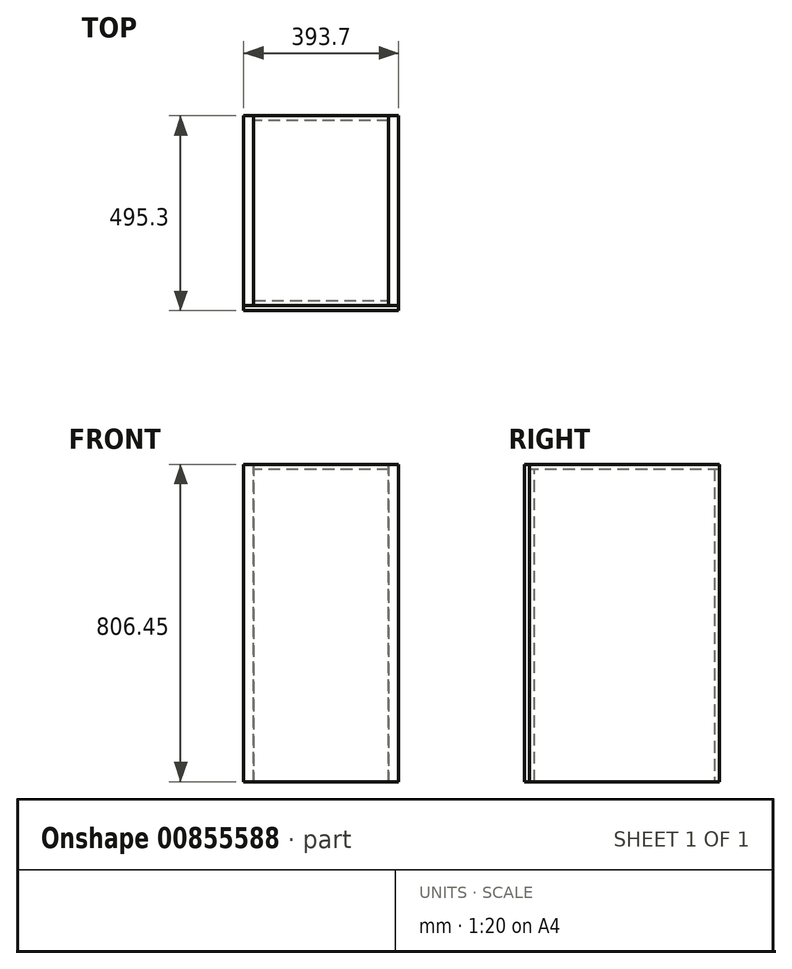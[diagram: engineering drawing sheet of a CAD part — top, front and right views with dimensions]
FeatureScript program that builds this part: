
annotation { "Feature Type Name" : "Feature", "Feature Type Description" : "" }
export const myFeature = defineFeature(function(context is Context, id is Id, definition is map)
    precondition{}
    {
        {
            var Q0;
            Q0=qCreatedBy(makeId("Front.planeOp"),FACE);
            var sketch = newSketch(context, id + "F0", { "sketchPlane" : qUnion([Q0])});
            skLineSegment(sketch, "E0.bottom", {"start": v(288.56, 543.22) * mm, "end": v(-105.14, 543.22) * mm});
            skLineSegment(sketch, "E0.top", {"start": v(288.56, -263.23) * mm, "end": v(-105.14, -263.23) * mm});
            skLineSegment(sketch, "E0.left", {"start": v(288.56, 543.22) * mm, "end": v(288.56, -263.23) * mm});
            skLineSegment(sketch, "E0.right", {"start": v(-105.14, 543.22) * mm, "end": v(-105.14, -263.23) * mm});
            skSolve(sketch);
        }
        {
            var Q0;
            Q0=makeQuery(id+"F0.imprint","IMPRINT",FACE,{"disambiguationData":[TD([[makeQuery(id+"F0.imprint","IMPRINT",EDGE,{"derivedFrom":sQuery(id+"F0.wireOp",EDGE,"E0.bottom")}),1.0]])]});
            var sketch = newSketch(context, id + "F1", { "sketchPlane" : qUnion([Q0])});
            skLineSegment(sketch, "E1.bottom", {"start": v(-105.14, 543.22) * mm, "end": v(-79.74, 543.22) * mm});
            skLineSegment(sketch, "E1.top", {"start": v(-105.14, -263.23) * mm, "end": v(-79.74, -263.23) * mm});
            skLineSegment(sketch, "E1.left", {"start": v(-105.14, 543.22) * mm, "end": v(-105.14, -263.23) * mm});
            skLineSegment(sketch, "E1.right", {"start": v(-79.74, 543.22) * mm, "end": v(-79.74, -263.23) * mm});
            skLineSegment(sketch, "E2.bottom", {"start": v(263.16, 543.22) * mm, "end": v(288.56, 543.22) * mm});
            skLineSegment(sketch, "E2.top", {"start": v(263.16, -263.23) * mm, "end": v(288.56, -263.23) * mm});
            skLineSegment(sketch, "E2.left", {"start": v(263.16, 543.22) * mm, "end": v(263.16, -263.23) * mm});
            skLineSegment(sketch, "E2.right", {"start": v(288.56, 543.22) * mm, "end": v(288.56, -263.23) * mm});
            skSolve(sketch);
        }
        {
            var Q0;
            Q0 = qSketchRegion(id + "F1", true);
            extrude(context, id + "F2", {"entities" : qUnion([Q0]), "depth" : 482.6 * mm, "offsetDistance" : 25.4 * mm});
        }
        {
            var Q0;
            Q0=makeQuery(id+"F2.opExtrude","CAP_FACE",FACE,{"disambiguationData":[OSD([sQuery(id+"F1.wireOp",EDGE,"E1.bottom"),sQuery(id+"F1.wireOp",EDGE,"E1.top"),sQuery(id+"F1.wireOp",EDGE,"E1.left"),sQuery(id+"F1.wireOp",EDGE,"E1.right")])],"isStart":false});
            var sketch = newSketch(context, id + "F3", { "sketchPlane" : qUnion([Q0])});
            skLineSegment(sketch, "E3.bottom", {"start": v(-79.74, 543.22) * mm, "end": v(263.16, 543.22) * mm});
            skLineSegment(sketch, "E3.top", {"start": v(-79.74, 530.52) * mm, "end": v(263.16, 530.52) * mm});
            skLineSegment(sketch, "E3.left", {"start": v(-79.74, 543.22) * mm, "end": v(-79.74, 530.52) * mm});
            skLineSegment(sketch, "E3.right", {"start": v(263.16, 543.22) * mm, "end": v(263.16, 530.52) * mm});
            skSolve(sketch);
        }
        {
            var Q0;
            Q0 = qSketchRegion(id + "F3", true);
            var Q1;
            Q1=makeQuery(id+"F2.opExtrude","CAP_FACE",FACE,{"disambiguationData":[OSD([sQuery(id+"F1.wireOp",EDGE,"E2.bottom"),sQuery(id+"F1.wireOp",EDGE,"E2.top"),sQuery(id+"F1.wireOp",EDGE,"E2.left"),sQuery(id+"F1.wireOp",EDGE,"E2.right")])],"isStart":true});
            extrude(context, id + "F4", {"entities" : qUnion([Q0]), "endBound" : BoundingType.UP_TO_SURFACE, "oppositeDirection" : true, "depth" : 25.4 * mm, "endBoundEntityFace" : qUnion([Q1]), "offsetDistance" : 25.4 * mm});
        }
        {
            var Q0;
            Q0=makeQuery(id+"F2.opExtrude","SWEPT_FACE",FACE,{"disambiguationData":[OSD([sQuery(id+"F1.wireOp",EDGE,"E1.top")])]});
            var sketch = newSketch(context, id + "F5", { "sketchPlane" : qUnion([Q0])});
            skLineSegment(sketch, "E4.bottom", {"start": v(-79.74, 12.7) * mm, "end": v(263.16, 12.7) * mm});
            skLineSegment(sketch, "E4.top", {"start": v(-79.74, 0) * mm, "end": v(263.16, 0) * mm});
            skLineSegment(sketch, "E4.left", {"start": v(-79.74, 12.7) * mm, "end": v(-79.74, 0) * mm});
            skLineSegment(sketch, "E4.right", {"start": v(263.16, 12.7) * mm, "end": v(263.16, 0) * mm});
            skSolve(sketch);
        }
        {
            var Q0;
            Q0 = qSketchRegion(id + "F5", true);
            var Q1;
            Q1=makeQuery(id+"F4.opExtrude","SWEPT_FACE",FACE,{"disambiguationData":[OSD([sQuery(id+"F3.wireOp",EDGE,"E3.top")])]});
            extrude(context, id + "F6", {"entities" : qUnion([Q0]), "endBound" : BoundingType.UP_TO_SURFACE, "oppositeDirection" : true, "depth" : 25.4 * mm, "endBoundEntityFace" : qUnion([Q1]), "offsetDistance" : 25.4 * mm});
        }
        {
            var Q0;
            Q0=makeQuery(id+"F4.opExtrude","SWEPT_FACE",FACE,{"disambiguationData":[OSD([sQuery(id+"F3.wireOp",EDGE,"E3.top")])]});
            var sketch = newSketch(context, id + "F7", { "sketchPlane" : qUnion([Q0])});
            skLineSegment(sketch, "E5.bottom", {"start": v(-79.74, 482.6) * mm, "end": v(263.16, 482.6) * mm});
            skLineSegment(sketch, "E5.top", {"start": v(-79.74, 469.9) * mm, "end": v(263.16, 469.9) * mm});
            skLineSegment(sketch, "E5.left", {"start": v(-79.74, 482.6) * mm, "end": v(-79.74, 469.9) * mm});
            skLineSegment(sketch, "E5.right", {"start": v(263.16, 482.6) * mm, "end": v(263.16, 469.9) * mm});
            skSolve(sketch);
        }
        {
            var Q0;
            Q0 = qSketchRegion(id + "F7", true);
            var Q1;
            Q1=makeQuery(id+"F2.opExtrude","SWEPT_FACE",FACE,{"disambiguationData":[OSD([sQuery(id+"F1.wireOp",EDGE,"E1.top")])]});
            extrude(context, id + "F8", {"entities" : qUnion([Q0]), "endBound" : BoundingType.UP_TO_SURFACE, "depth" : 25.4 * mm, "endBoundEntityFace" : qUnion([Q1]), "offsetDistance" : 25.4 * mm});
        }
        {
            var Q0;
            Q0 = qSketchRegion(id + "F0", true);
            extrude(context, id + "F9", {"entities" : qUnion([Q0]), "depth" : 495.3 * mm, "offsetDistance" : 25.4 * mm});
        }
    });
